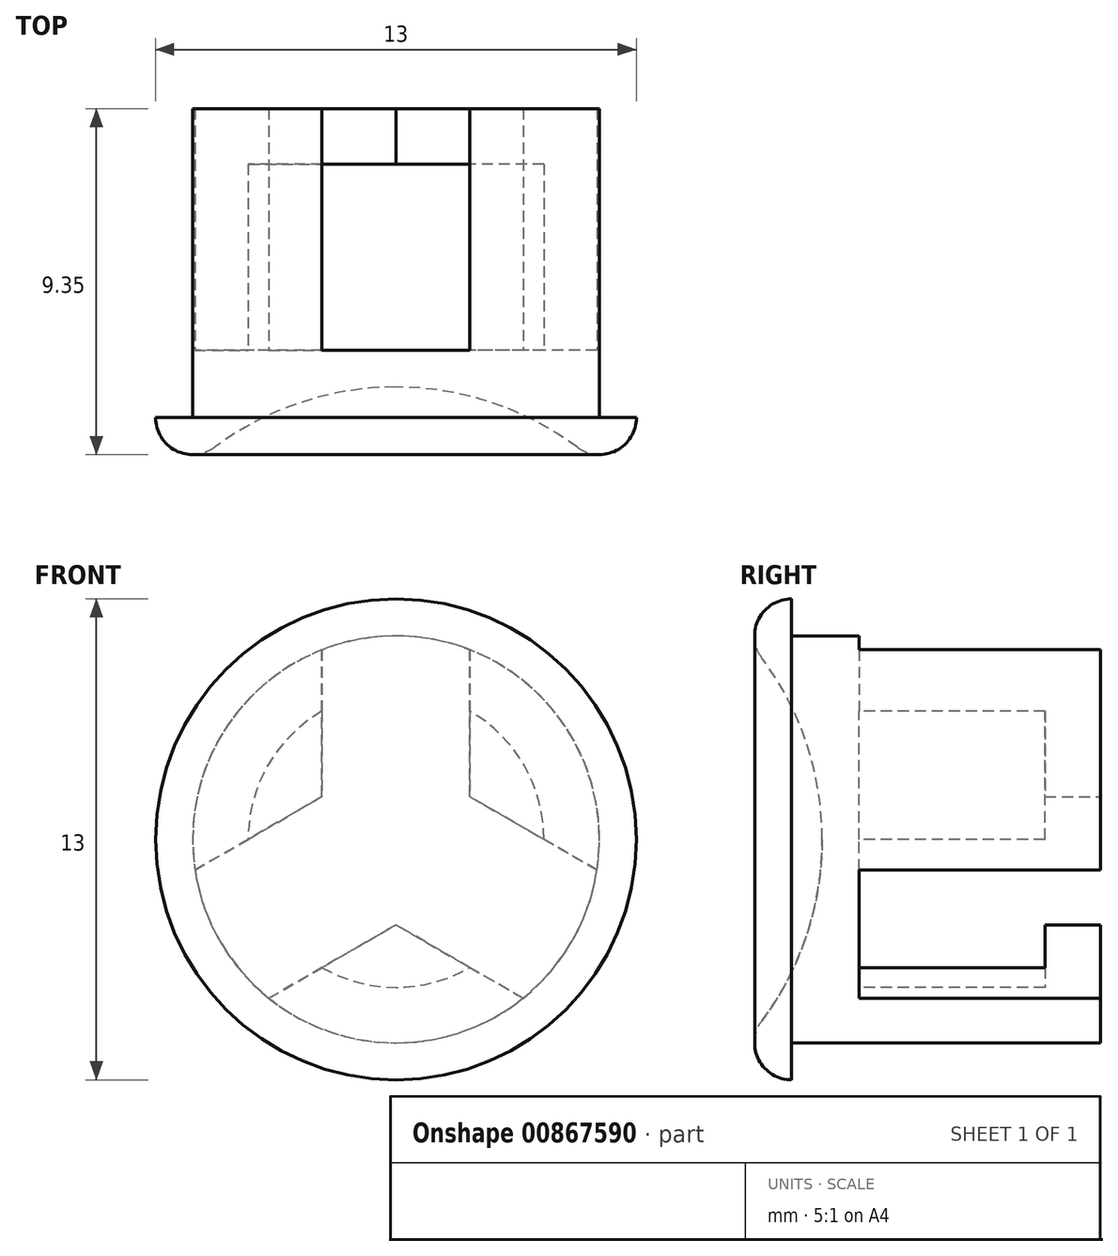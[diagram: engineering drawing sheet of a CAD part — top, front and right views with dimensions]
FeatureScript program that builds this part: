
annotation { "Feature Type Name" : "Feature", "Feature Type Description" : "" }
export const myFeature = defineFeature(function(context is Context, id is Id, definition is map)
    precondition{}
    {
        {
            var Q0;
            Q0=qCreatedBy(makeId("Right.planeOp"),FACE);
            var sketch = newSketch(context, id + "F0", { "sketchPlane" : qUnion([Q0])});
            skCircle(sketch, "E0", {"center": v(0, 0) * mm, "radius": 12 * mm});
            skSolve(sketch);
        }
        {
            var Q0;
            Q0=qCreatedBy(makeId("Right.planeOp"),FACE);
            var sketch = newSketch(context, id + "F1", { "sketchPlane" : qUnion([Q0])});
            skCircle(sketch, "E1.0", {"center": v(0, 0) * mm, "radius": 12 * mm, "construction": true});
            skLineSegment(sketch, "E2", {"start": v(-10.67, 5.5) * mm, "end": v(-10.67, -5.5) * mm, "construction": true});
            skLineSegment(sketch, "E3", {"start": v(-12, 0) * mm, "end": v(12, 0) * mm, "construction": true});
            skPoint(sketch, "E3.startSnap0", {"position": v(-10.67, 0) * mm});
            skCircle(sketch, "E4", {"center": v(0, 0) * mm, "radius": 11 * mm, "construction": true});
            skPoint(sketch, "E5", {"position": v(11, 0) * mm});
            skLineSegment(sketch, "E6", {"start": v(-10.67, 5.5) * mm, "end": v(-9.53, 5.5) * mm, "construction": true});
            skLineSegment(sketch, "E7", {"start": v(-9.53, 5.5) * mm, "end": v(-9.53, 0) * mm, "construction": true});
            skArc(sketch, "E8", {"start": v(-7.53, 0) * mm, "mid": v(-7.94, 2.58) * mm, "end": v(-9.15, 4.9) * mm});
            skLineSegment(sketch, "E9", {"start": v(-7.53, 0) * mm, "end": v(-7.53, 8.02) * mm, "construction": true});
            skArc(sketch, "E10", {"start": v(-9.15, 4.9) * mm, "mid": v(-9.25, 5.95) * mm, "end": v(-8.35, 6.5) * mm});
            skLineSegment(sketch, "E11", {"start": v(-8.35, 6.5) * mm, "end": v(-7.53, 6.5) * mm, "construction": true});
            skLineSegment(sketch, "E12", {"start": v(-8.35, 6.5) * mm, "end": v(-8.35, 5.5) * mm});
            skLineSegment(sketch, "E13", {"start": v(-6.53, 4) * mm, "end": v(-6.53, 0) * mm});
            skLineSegment(sketch, "E14", {"start": v(0, 0) * mm, "end": v(0, 5.5) * mm});
            skLineSegment(sketch, "E15", {"start": v(0, 0) * mm, "end": v(-1.5, 0) * mm});
            skLineSegment(sketch, "E16", {"start": v(-1.5, 0) * mm, "end": v(-1.5, 4) * mm});
            skLineSegment(sketch, "E17", {"start": v(-6.53, 4) * mm, "end": v(-1.5, 4) * mm});
            skLineSegment(sketch, "E18", {"start": v(-8.35, 5.5) * mm, "end": v(0, 5.5) * mm});
            skLineSegment(sketch, "E19", {"start": v(-7.53, 0) * mm, "end": v(-6.53, 0) * mm});
            skSolve(sketch);
        }
        {
            var Q0;
            Q0 = qSketchRegion(id + "F1", true);
            var Q1;
            Q1=sQuery(id+"F1.wireOp",EDGE,"E3");
            revolve(context, id + "F2", {"surfaceOperationType" : NewSurfaceOperationType.NEW, "entities" : qUnion([Q0]), "axis" : qUnion([Q1]), "revolveType" : RevolveType.FULL});
        }
        {
            var Q0;
            Q0=makeQuery(id+"F2.opRevolve","SWEPT_FACE",FACE,{"disambiguationData":[OSD([sQuery(id+"F1.wireOp",EDGE,"E14")])]});
            var sketch = newSketch(context, id + "F3", { "sketchPlane" : qUnion([Q0])});
            skLineSegment(sketch, "E20", {"start": v(0, 0) * mm, "end": v(0, 5.5) * mm, "construction": true});
            skArc(sketch, "E21.0.endCap", {"start": v(-2, 5.5) * mm, "mid": v(0, 7.5) * mm, "end": v(2, 5.5) * mm});
            skLineSegment(sketch, "E21.0.left", {"start": v(-2, 1.15) * mm, "end": v(-2, 5.5) * mm});
            skLineSegment(sketch, "E21.0.right", {"start": v(2, 1.15) * mm, "end": v(2, 5.5) * mm});
            skLineSegment(sketch, "E22.1.0", {"start": v(0, -2.3) * mm, "end": v(-3.76, -4.48) * mm});
            skArc(sketch, "E22.1.1", {"start": v(-3.76, -4.48) * mm, "mid": v(-6.5, -3.75) * mm, "end": v(-5.76, -1.02) * mm});
            skLineSegment(sketch, "E22.1.2", {"start": v(-2, 1.15) * mm, "end": v(-5.76, -1.02) * mm});
            skLineSegment(sketch, "E22.1.3", {"start": v(0, 0) * mm, "end": v(-4.76, -2.75) * mm, "construction": true});
            skLineSegment(sketch, "E22.2.0", {"start": v(2, 1.15) * mm, "end": v(5.76, -1.02) * mm});
            skArc(sketch, "E22.2.1", {"start": v(5.76, -1.02) * mm, "mid": v(6.5, -3.75) * mm, "end": v(3.76, -4.48) * mm});
            skLineSegment(sketch, "E22.2.2", {"start": v(0, -2.3) * mm, "end": v(3.76, -4.48) * mm});
            skLineSegment(sketch, "E22.2.3", {"start": v(0, 0) * mm, "end": v(4.76, -2.75) * mm, "construction": true});
            skPoint(sketch, "E22.center", {"position": v(0, 0) * mm});
            skPoint(sketch, "E23.orphan", {"position": v(1.06, 1.7) * mm});
            skPoint(sketch, "E24.orphan", {"position": v(-1, 1.73) * mm});
            skPoint(sketch, "E25.orphan", {"position": v(-1, -1.73) * mm});
            skPoint(sketch, "E26.orphan", {"position": v(0.94, -1.77) * mm});
            skPoint(sketch, "E27.orphan", {"position": v(-2, 0.07) * mm});
            skPoint(sketch, "E28.orphan", {"position": v(2, 0) * mm});
            skSolve(sketch);
        }
        {
            var Q0;
            Q0 = qSketchRegion(id + "F3", true);
            var Q1;
            Q1=makeQuery(id+"F2.opRevolve","SWEPT_FACE",FACE,{"disambiguationData":[OSD([sQuery(id+"F1.wireOp",EDGE,"E13")])]});
            extrude(context, id + "F4", {"entities" : qUnion([Q0]), "operationType" : NewBodyOperationType.REMOVE, "endBound" : BoundingType.UP_TO_SURFACE, "oppositeDirection" : true, "depth" : 25 * mm, "endBoundEntityFace" : qUnion([Q1]), "offsetDistance" : 25 * mm});
        }
    });
